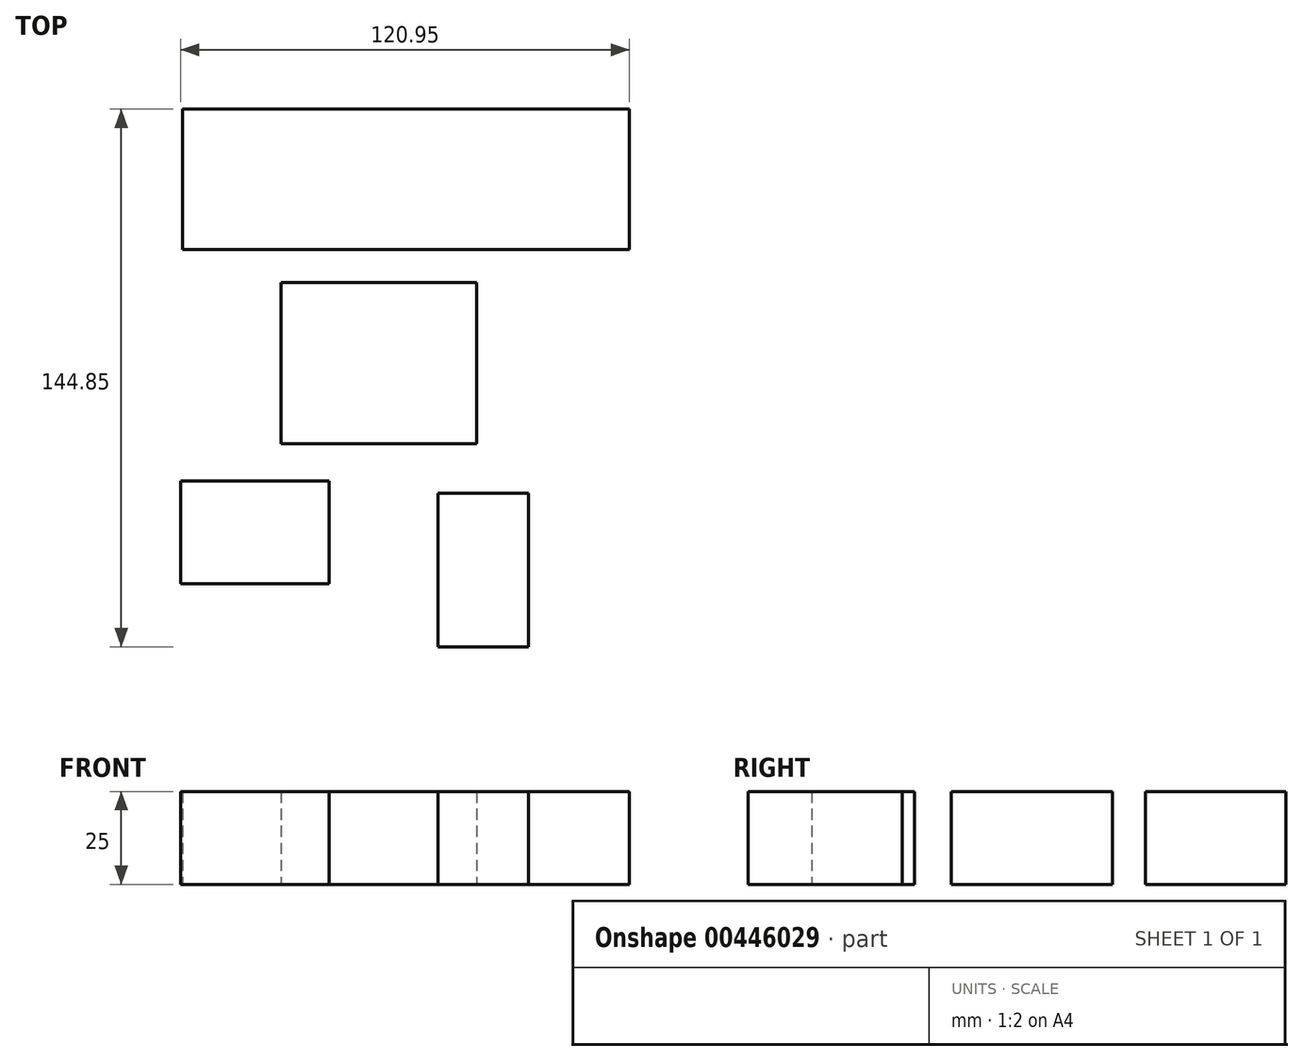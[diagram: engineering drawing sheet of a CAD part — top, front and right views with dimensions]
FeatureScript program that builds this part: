
annotation { "Feature Type Name" : "Feature", "Feature Type Description" : "" }
export const myFeature = defineFeature(function(context is Context, id is Id, definition is map)
    precondition{}
    {
        {
            var Q0;
            Q0=qCreatedBy(makeId("Top.planeOp"),FACE);
            var sketch = newSketch(context, id + "F0", { "sketchPlane" : qUnion([Q0])});
            skLineSegment(sketch, "E0.bottom", {"start": v(24.84, -15.92) * mm, "end": v(-27.83, -15.92) * mm});
            skLineSegment(sketch, "E0.top", {"start": v(24.84, 27.6) * mm, "end": v(-27.83, 27.6) * mm});
            skLineSegment(sketch, "E0.left", {"start": v(24.84, -15.92) * mm, "end": v(24.84, 27.6) * mm});
            skLineSegment(sketch, "E0.right", {"start": v(-27.83, -15.92) * mm, "end": v(-27.83, 27.6) * mm});
            skLineSegment(sketch, "E1.bottom", {"start": v(-54.86, -25.85) * mm, "end": v(-14.86, -25.85) * mm});
            skLineSegment(sketch, "E1.top", {"start": v(-54.86, -53.55) * mm, "end": v(-14.86, -53.55) * mm});
            skLineSegment(sketch, "E1.left", {"start": v(-54.86, -25.85) * mm, "end": v(-54.86, -53.55) * mm});
            skLineSegment(sketch, "E1.right", {"start": v(-14.86, -25.85) * mm, "end": v(-14.86, -53.55) * mm});
            skLineSegment(sketch, "E2.bottom", {"start": v(-54.38, 74.26) * mm, "end": v(66.09, 74.26) * mm});
            skLineSegment(sketch, "E2.top", {"start": v(-54.38, 36.4) * mm, "end": v(66.09, 36.4) * mm});
            skLineSegment(sketch, "E2.left", {"start": v(-54.38, 74.26) * mm, "end": v(-54.38, 36.4) * mm});
            skLineSegment(sketch, "E2.right", {"start": v(66.09, 74.26) * mm, "end": v(66.09, 36.4) * mm});
            skLineSegment(sketch, "E3.bottom", {"start": v(14.5, -29.17) * mm, "end": v(38.87, -29.17) * mm});
            skLineSegment(sketch, "E3.top", {"start": v(14.5, -70.59) * mm, "end": v(38.87, -70.59) * mm});
            skLineSegment(sketch, "E3.left", {"start": v(14.5, -29.17) * mm, "end": v(14.5, -70.59) * mm});
            skLineSegment(sketch, "E3.right", {"start": v(38.87, -29.17) * mm, "end": v(38.87, -70.59) * mm});
            skSolve(sketch);
        }
        {
            var Q0;
            Q0 = qSketchRegion(id + "F0", true);
            extrude(context, id + "F1", {"entities" : qUnion([Q0]), "depth" : 25 * mm});
        }
    });
